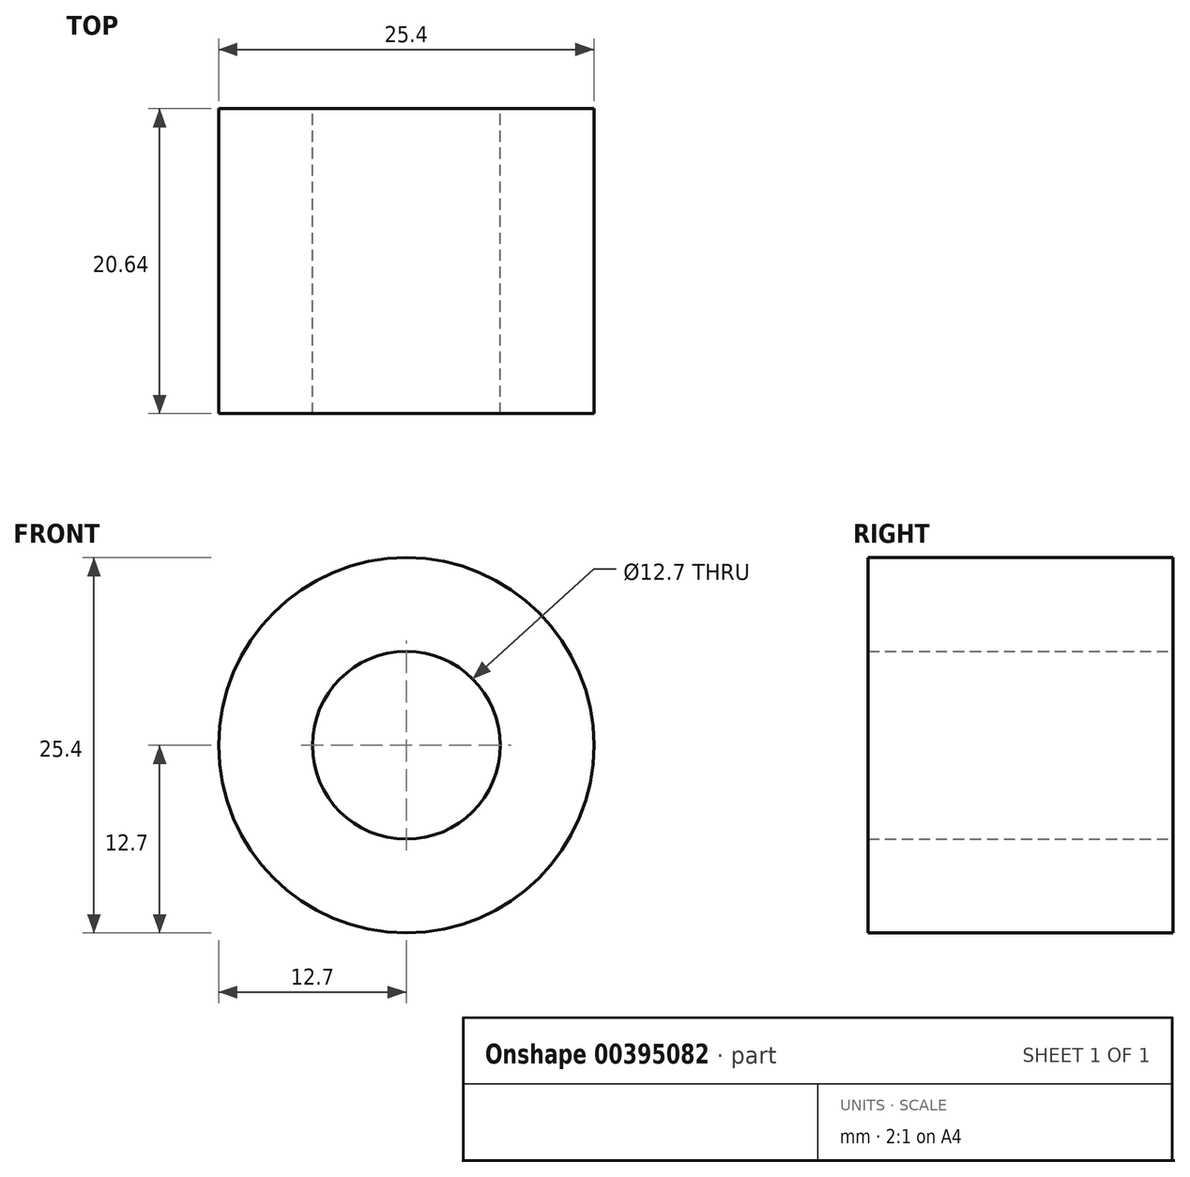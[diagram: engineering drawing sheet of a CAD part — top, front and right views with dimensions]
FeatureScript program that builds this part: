
annotation { "Feature Type Name" : "Feature", "Feature Type Description" : "" }
export const myFeature = defineFeature(function(context is Context, id is Id, definition is map)
    precondition{}
    {
        {
            var Q0;
            Q0=qCreatedBy(makeId("Right.planeOp"),FACE);
            var sketch = newSketch(context, id + "F0", { "sketchPlane" : qUnion([Q0])});
            skLineSegment(sketch, "E0.bottom", {"start": v(8.73, 6.35) * mm, "end": v(-8.73, 6.35) * mm});
            skLineSegment(sketch, "E0.top", {"start": v(8.73, -6.35) * mm, "end": v(-8.73, -6.35) * mm});
            skLineSegment(sketch, "E0.left", {"start": v(8.73, 6.35) * mm, "end": v(8.73, -6.35) * mm, "construction": true});
            skPoint(sketch, "E0.middle", {"position": v(0, 0) * mm});
            skFitSpline(sketch, "E1", {"points": [v(-23.02, 0) * mm, v(-8.73, 6.35) * mm], "startDerivative": vector(-5.85, -9.98) * mm, "endDerivative": vector(35.52, 0) * mm});
            skFitSpline(sketch, "E2", {"points": [v(-23.02, 0) * mm, v(-8.73, -6.35) * mm], "startDerivative": vector(-5.85, 9.98) * mm, "endDerivative": vector(35.52, 0) * mm});
            skLineSegment(sketch, "E3", {"start": v(32.55, 0) * mm, "end": v(-39.38, 0) * mm});
            skLineSegment(sketch, "E4.bottom", {"start": v(-21.43, 1.59) * mm, "end": v(-27.78, 1.59) * mm});
            skLineSegment(sketch, "E4.top", {"start": v(-21.43, -1.59) * mm, "end": v(-27.78, -1.59) * mm});
            skLineSegment(sketch, "E4.left", {"start": v(-21.43, 1.59) * mm, "end": v(-21.43, -1.59) * mm, "construction": true});
            skLineSegment(sketch, "E4.right", {"start": v(-27.78, 1.59) * mm, "end": v(-27.78, -1.59) * mm, "construction": true});
            skLineSegment(sketch, "E5.bottom", {"start": v(-8.73, 6.35) * mm, "end": v(8.73, 6.35) * mm});
            skLineSegment(sketch, "E5.top", {"start": v(-8.73, 12.7) * mm, "end": v(8.73, 12.7) * mm});
            skLineSegment(sketch, "E5.left", {"start": v(-8.73, 6.35) * mm, "end": v(-8.73, 12.7) * mm});
            skLineSegment(sketch, "E5.right", {"start": v(8.73, 6.35) * mm, "end": v(8.73, 12.7) * mm});
            skLineSegment(sketch, "E6.MirrorCS", {"start": v(8.73, -6.35) * mm, "end": v(8.73, -12.7) * mm});
            skLineSegment(sketch, "E7.MirrorCS", {"start": v(-8.73, -6.35) * mm, "end": v(-8.73, -12.7) * mm});
            skLineSegment(sketch, "E8.MirrorCS", {"start": v(-8.73, -12.7) * mm, "end": v(8.73, -12.7) * mm});
            skFitSpline(sketch, "E9", {"points": [v(-27.78, 1.59) * mm, v(-8.73, 12.7) * mm], "startDerivative": vector(9.44, 21.23) * mm, "endDerivative": vector(22.03, 0) * mm});
            skFitSpline(sketch, "E10", {"points": [v(-27.78, -1.59) * mm, v(-8.73, -12.7) * mm], "startDerivative": vector(9.44, -21.23) * mm, "endDerivative": vector(22.03, 0) * mm});
            skLineSegment(sketch, "E11", {"start": v(-23.02, -1.59) * mm, "end": v(-23.02, 1.59) * mm, "construction": true});
            skLineSegment(sketch, "E12", {"start": v(-24.6, -1.59) * mm, "end": v(-24.6, 1.59) * mm, "construction": true});
            skLineSegment(sketch, "E13", {"start": v(7.14, 6.35) * mm, "end": v(7.14, -6.35) * mm, "construction": true});
            skPoint(sketch, "E14.orphan", {"position": v(-5.56, 6.35) * mm});
            skLineSegment(sketch, "E15.bottom", {"start": v(-8.73, -6.35) * mm, "end": v(-5.56, -6.35) * mm});
            skLineSegment(sketch, "E15.top", {"start": v(-8.73, 6.35) * mm, "end": v(-5.56, 6.35) * mm});
            skLineSegment(sketch, "E15.left", {"start": v(-8.73, -6.35) * mm, "end": v(-8.73, 6.35) * mm, "construction": true});
            skLineSegment(sketch, "E15.right", {"start": v(-5.56, -6.35) * mm, "end": v(-5.56, 6.35) * mm, "construction": true});
            skLineSegment(sketch, "E16.bottom", {"start": v(8.73, 6.35) * mm, "end": v(11.9, 6.35) * mm});
            skLineSegment(sketch, "E16.top", {"start": v(8.73, 12.7) * mm, "end": v(11.9, 12.7) * mm});
            skLineSegment(sketch, "E16.right", {"start": v(11.9, 6.35) * mm, "end": v(11.9, 12.7) * mm});
            skLineSegment(sketch, "E17", {"start": v(11.9, 6.35) * mm, "end": v(11.9, -6.35) * mm, "construction": true});
            skLineSegment(sketch, "E18.bottom", {"start": v(11.9, -6.35) * mm, "end": v(8.73, -6.35) * mm});
            skLineSegment(sketch, "E18.top", {"start": v(11.9, -12.7) * mm, "end": v(8.73, -12.7) * mm});
            skLineSegment(sketch, "E18.left", {"start": v(11.9, -6.35) * mm, "end": v(11.9, -12.7) * mm});
            skLineSegment(sketch, "E19", {"start": v(8.73, 1.59) * mm, "end": v(11.9, 1.59) * mm, "construction": true});
            skLineSegment(sketch, "E20.MirrorCS", {"start": v(8.73, -1.59) * mm, "end": v(11.9, -1.59) * mm, "construction": true});
            skSolve(sketch);
        }
        {
            var Q0;
            Q0 = qSketchRegion(id + "F0", true);
            var Q1;
            Q1=sQuery(id+"F0.wireOp",EDGE,"E3");
            revolve(context, id + "F1", {"entities" : qUnion([Q0]), "axis" : qUnion([Q1]), "revolveType" : RevolveType.FULL});
        }
        {
            var Q0;
            Q0=makeQuery(id+"F1.opRevolve","SWEPT_BODY",BODY,{"disambiguationData":[OSD([sQuery(id+"F0.wireOp",EDGE,"E1"),sQuery(id+"F0.wireOp",EDGE,"E4.bottom"),sQuery(id+"F0.wireOp",EDGE,"E5.bottom"),sQuery(id+"F0.wireOp",EDGE,"E5.top"),sQuery(id+"F0.wireOp",EDGE,"E9"),sQuery(id+"F0.wireOp",EDGE,"E15.top"),sQuery(id+"F0.wireOp",EDGE,"E16.bottom"),sQuery(id+"F0.wireOp",EDGE,"E16.top"),sQuery(id+"F0.wireOp",EDGE,"E16.right")])]});
            deleteBodies(context, id + "F2", {"entities" : qUnion([Q0])});
        }
    });
